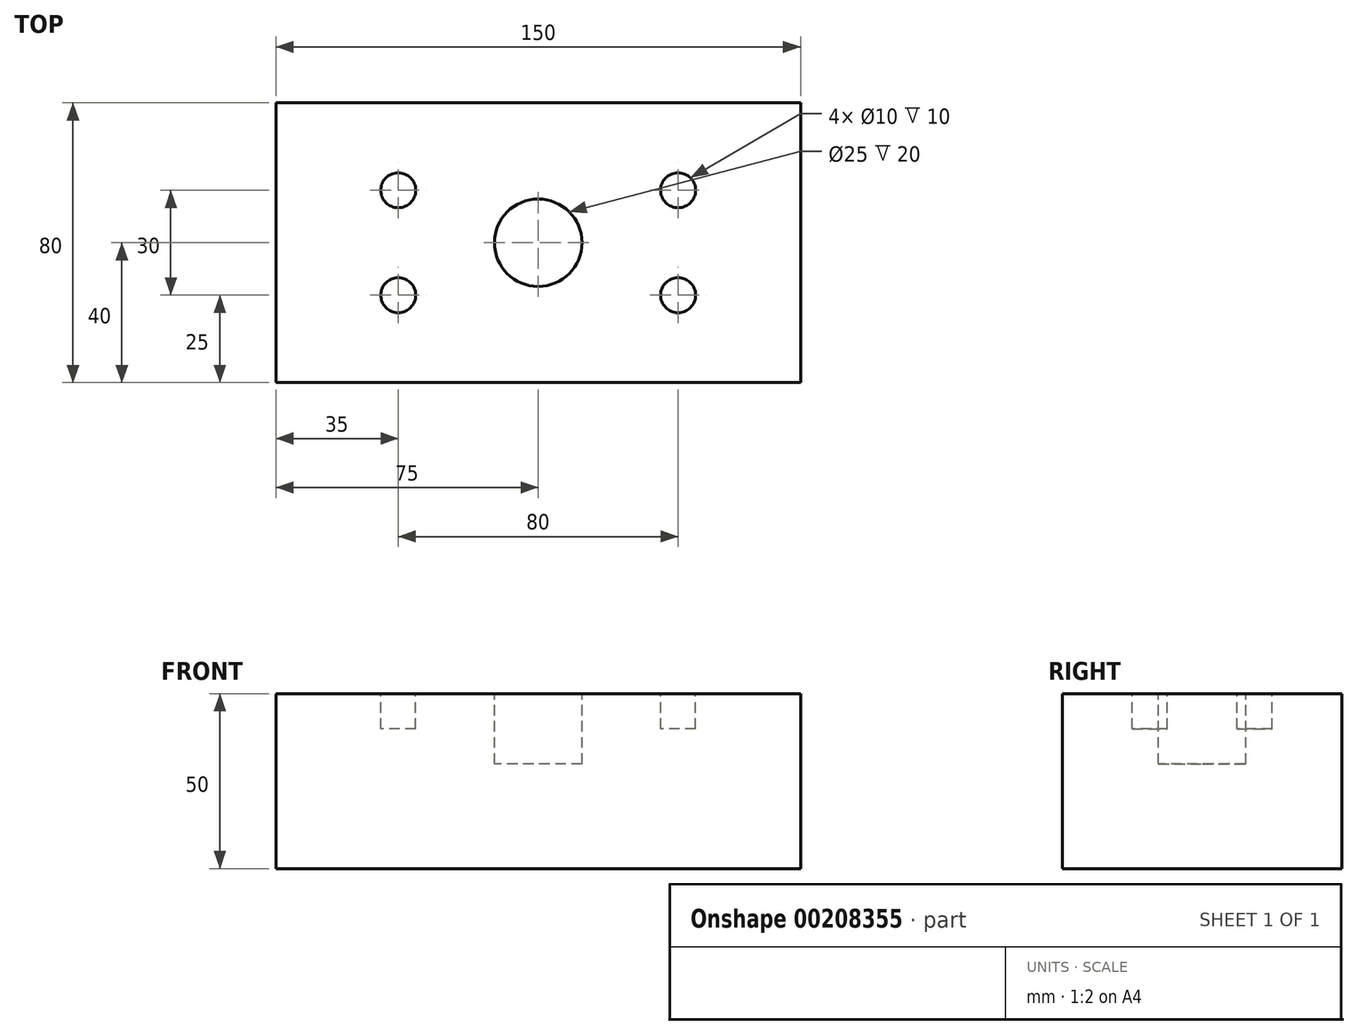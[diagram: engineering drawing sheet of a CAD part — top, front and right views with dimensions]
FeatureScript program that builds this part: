
annotation { "Feature Type Name" : "Feature", "Feature Type Description" : "" }
export const myFeature = defineFeature(function(context is Context, id is Id, definition is map)
    precondition{}
    {
        {
            var Q0;
            Q0=qCreatedBy(makeId("Top.planeOp"),FACE);
            var sketch = newSketch(context, id + "F0", { "sketchPlane" : qUnion([Q0])});
            skLineSegment(sketch, "E0.bottom", {"start": v(0, 0) * mm, "end": v(150, 0) * mm});
            skLineSegment(sketch, "E0.top", {"start": v(0, 80) * mm, "end": v(150, 80) * mm});
            skLineSegment(sketch, "E0.left", {"start": v(0, 0) * mm, "end": v(0, 80) * mm});
            skLineSegment(sketch, "E0.right", {"start": v(150, 0) * mm, "end": v(150, 80) * mm});
            skLineSegment(sketch, "E1", {"start": v(75, 80) * mm, "end": v(75, 0) * mm, "construction": true});
            skLineSegment(sketch, "E2", {"start": v(0, 40) * mm, "end": v(150, 40) * mm, "construction": true});
            skSolve(sketch);
        }
        {
            var Q0;
            Q0=makeQuery(id+"F0.imprint","IMPRINT",FACE,{"disambiguationData":[TD([[makeQuery(id+"F0.imprint","IMPRINT",EDGE,{"derivedFrom":sQuery(id+"F0.wireOp",EDGE,"E0.bottom")}),1.0]])]});
            extrude(context, id + "F1", {"entities" : qUnion([Q0]), "oppositeDirection" : true, "depth" : 50 * mm});
        }
        {
            var Q0;
            Q0=makeQuery(id+"F1.opExtrude","CAP_FACE",FACE,{"disambiguationData":[OSD([sQuery(id+"F0.wireOp",EDGE,"E0.bottom"),sQuery(id+"F0.wireOp",EDGE,"E0.top"),sQuery(id+"F0.wireOp",EDGE,"E0.left"),sQuery(id+"F0.wireOp",EDGE,"E0.right")])],"isStart":true});
            var sketch = newSketch(context, id + "F2", { "sketchPlane" : qUnion([Q0])});
            skLineSegment(sketch, "E3.0", {"start": v(0, 40) * mm, "end": v(150, 40) * mm, "construction": true});
            skLineSegment(sketch, "E4.0", {"start": v(75, 80) * mm, "end": v(75, 0) * mm, "construction": true});
            skCircle(sketch, "E5", {"center": v(75, 40) * mm, "radius": 12.5 * mm});
            skCircle(sketch, "E6", {"center": v(115, 55) * mm, "radius": 5 * mm});
            skCircle(sketch, "E7", {"center": v(115, 25) * mm, "radius": 5 * mm});
            skCircle(sketch, "E8", {"center": v(35, 25) * mm, "radius": 5 * mm});
            skCircle(sketch, "E9", {"center": v(35, 55) * mm, "radius": 5 * mm});
            skSolve(sketch);
        }
        {
            var Q0;
            Q0=makeQuery(id+"F2.imprint","IMPRINT",FACE,{"disambiguationData":[TD([[makeQuery(id+"F2.imprint","IMPRINT",EDGE,{"derivedFrom":sQuery(id+"F2.wireOp",EDGE,"E5")}),1.0]])]});
            extrude(context, id + "F3", {"entities" : qUnion([Q0]), "operationType" : NewBodyOperationType.REMOVE, "oppositeDirection" : true, "depth" : 20 * mm});
        }
        {
            var Q0;
            Q0=makeQuery(id+"F2.imprint","IMPRINT",FACE,{"disambiguationData":[TD([[makeQuery(id+"F2.imprint","IMPRINT",EDGE,{"derivedFrom":sQuery(id+"F2.wireOp",EDGE,"E9")}),1.0]])]});
            var Q1;
            Q1=makeQuery(id+"F2.imprint","IMPRINT",FACE,{"disambiguationData":[TD([[makeQuery(id+"F2.imprint","IMPRINT",EDGE,{"derivedFrom":sQuery(id+"F2.wireOp",EDGE,"E6")}),1.0]])]});
            var Q2;
            Q2=makeQuery(id+"F2.imprint","IMPRINT",FACE,{"disambiguationData":[TD([[makeQuery(id+"F2.imprint","IMPRINT",EDGE,{"derivedFrom":sQuery(id+"F2.wireOp",EDGE,"E8")}),1.0]])]});
            var Q3;
            Q3=makeQuery(id+"F2.imprint","IMPRINT",FACE,{"disambiguationData":[TD([[makeQuery(id+"F2.imprint","IMPRINT",EDGE,{"derivedFrom":sQuery(id+"F2.wireOp",EDGE,"E7")}),1.0]])]});
            extrude(context, id + "F4", {"entities" : qUnion([Q0, Q1, Q2, Q3]), "operationType" : NewBodyOperationType.REMOVE, "oppositeDirection" : true, "depth" : 10 * mm});
        }
    });
